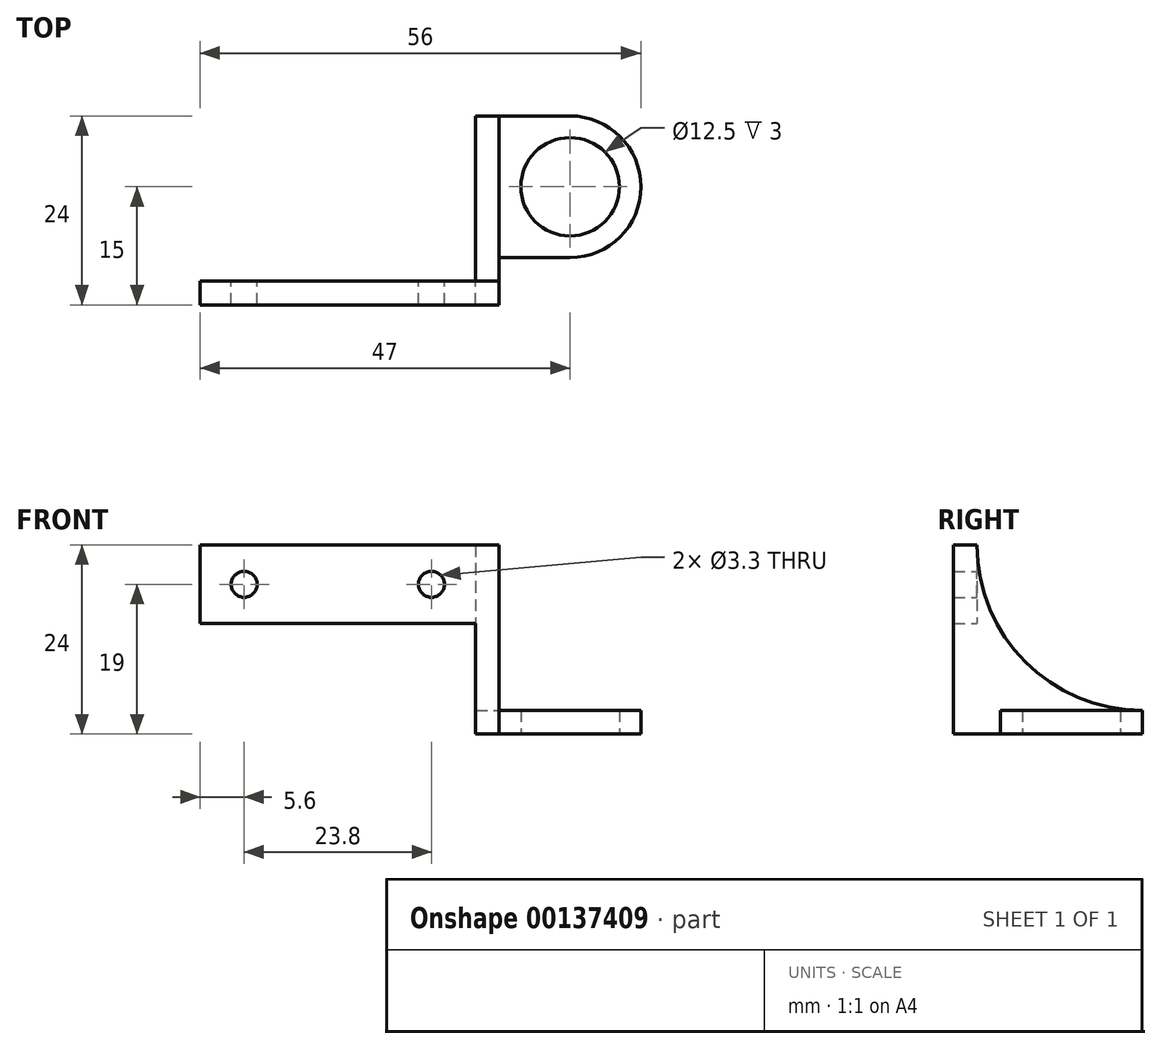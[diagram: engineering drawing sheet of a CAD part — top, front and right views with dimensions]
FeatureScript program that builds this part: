
annotation { "Feature Type Name" : "Feature", "Feature Type Description" : "" }
export const myFeature = defineFeature(function(context is Context, id is Id, definition is map)
    precondition{}
    {
        {
            var Q0;
            Q0=qCreatedBy(makeId("Front.planeOp"),FACE);
            var sketch = newSketch(context, id + "F0", { "sketchPlane" : qUnion([Q0])});
            skLineSegment(sketch, "E0.bottom", {"start": v(-17.5, 5) * mm, "end": v(17.5, 5) * mm});
            skLineSegment(sketch, "E0.top", {"start": v(-17.5, -5) * mm, "end": v(17.5, -5) * mm});
            skLineSegment(sketch, "E0.left", {"start": v(-17.5, 5) * mm, "end": v(-17.5, -5) * mm});
            skLineSegment(sketch, "E0.right", {"start": v(17.5, 5) * mm, "end": v(17.5, -5) * mm});
            skCircle(sketch, "E1", {"center": v(-11.9, 0) * mm, "radius": 1.65 * mm});
            skCircle(sketch, "E2", {"center": v(11.9, 0) * mm, "radius": 1.65 * mm});
            skSolve(sketch);
        }
        {
            var Q0;
            Q0=makeQuery(id+"F0.imprint","IMPRINT",FACE,{"disambiguationData":[TD([[makeQuery(id+"F0.imprint","IMPRINT",EDGE,{"derivedFrom":sQuery(id+"F0.wireOp",EDGE,"E0.bottom")}),-1.0]])]});
            extrude(context, id + "F1", {"entities" : qUnion([Q0]), "depth" : 3 * mm});
        }
        {
            var Q0;
            Q0=makeQuery(id+"F1.opExtrude","SWEPT_FACE",FACE,{"disambiguationData":[OSD([sQuery(id+"F0.wireOp",EDGE,"E0.right")])]});
            var sketch = newSketch(context, id + "F2", { "sketchPlane" : qUnion([Q0])});
            skLineSegment(sketch, "E3.bottom", {"start": v(-3, 5) * mm, "end": v(21, 5) * mm});
            skLineSegment(sketch, "E3.top", {"start": v(-3, -19) * mm, "end": v(21, -19) * mm});
            skLineSegment(sketch, "E3.left", {"start": v(-3, 5) * mm, "end": v(-3, -19) * mm});
            skLineSegment(sketch, "E3.right", {"start": v(21, 5) * mm, "end": v(21, -19) * mm});
            skSolve(sketch);
        }
        {
            var Q0;
            Q0=qSketchRegion(id+"F2",true);
            extrude(context, id + "F3", {"entities" : qUnion([Q0]), "operationType" : NewBodyOperationType.ADD, "depth" : 3 * mm});
        }
        {
            var Q0;
            Q0=makeQuery(id+"F3.opExtrude","SWEPT_FACE",FACE,{"disambiguationData":[OSD([sQuery(id+"F2.wireOp",EDGE,"E3.top")])]});
            var sketch = newSketch(context, id + "F4", { "sketchPlane" : qUnion([Q0])});
            skArc(sketch, "E4", {"start": v(29.5, -21) * mm, "mid": v(38.5, -12) * mm, "end": v(29.5, -3) * mm});
            skCircle(sketch, "E5", {"center": v(29.5, -12) * mm, "radius": 6.25 * mm});
            skLineSegment(sketch, "E6", {"start": v(20.5, -21) * mm, "end": v(29.5, -21) * mm});
            skLineSegment(sketch, "E7", {"start": v(20.5, -3) * mm, "end": v(29.5, -3) * mm});
            skSolve(sketch);
        }
        {
            var Q0;
            Q0=makeQuery(id+"F4.imprint","IMPRINT",FACE,{"disambiguationData":[TD([[makeQuery(id+"F4.imprint","IMPRINT",EDGE,{"derivedFrom":sQuery(id+"F4.wireOp",EDGE,"E4")}),1.0]])]});
            extrude(context, id + "F5", {"entities" : qUnion([Q0]), "operationType" : NewBodyOperationType.ADD, "oppositeDirection" : true, "depth" : 3 * mm});
        }
        {
            var Q0;
            Q0=makeQuery(id+"F3.opExtrude","CAP_FACE",FACE,{"disambiguationData":[OSD([sQuery(id+"F2.wireOp",EDGE,"E3.bottom"),sQuery(id+"F2.wireOp",EDGE,"E3.top"),sQuery(id+"F2.wireOp",EDGE,"E3.left"),sQuery(id+"F2.wireOp",EDGE,"E3.right")])],"isStart":false});
            var sketch = newSketch(context, id + "F6", { "sketchPlane" : qUnion([Q0])});
            skCircle(sketch, "E8", {"center": v(21, 5) * mm, "radius": 21 * mm});
            skSolve(sketch);
        }
        {
            var Q0;
            Q0=qSketchRegion(id+"F6",true);
            extrude(context, id + "F7", {"entities" : qUnion([Q0]), "operationType" : NewBodyOperationType.REMOVE, "oppositeDirection" : true, "depth" : 3 * mm});
        }
    });
